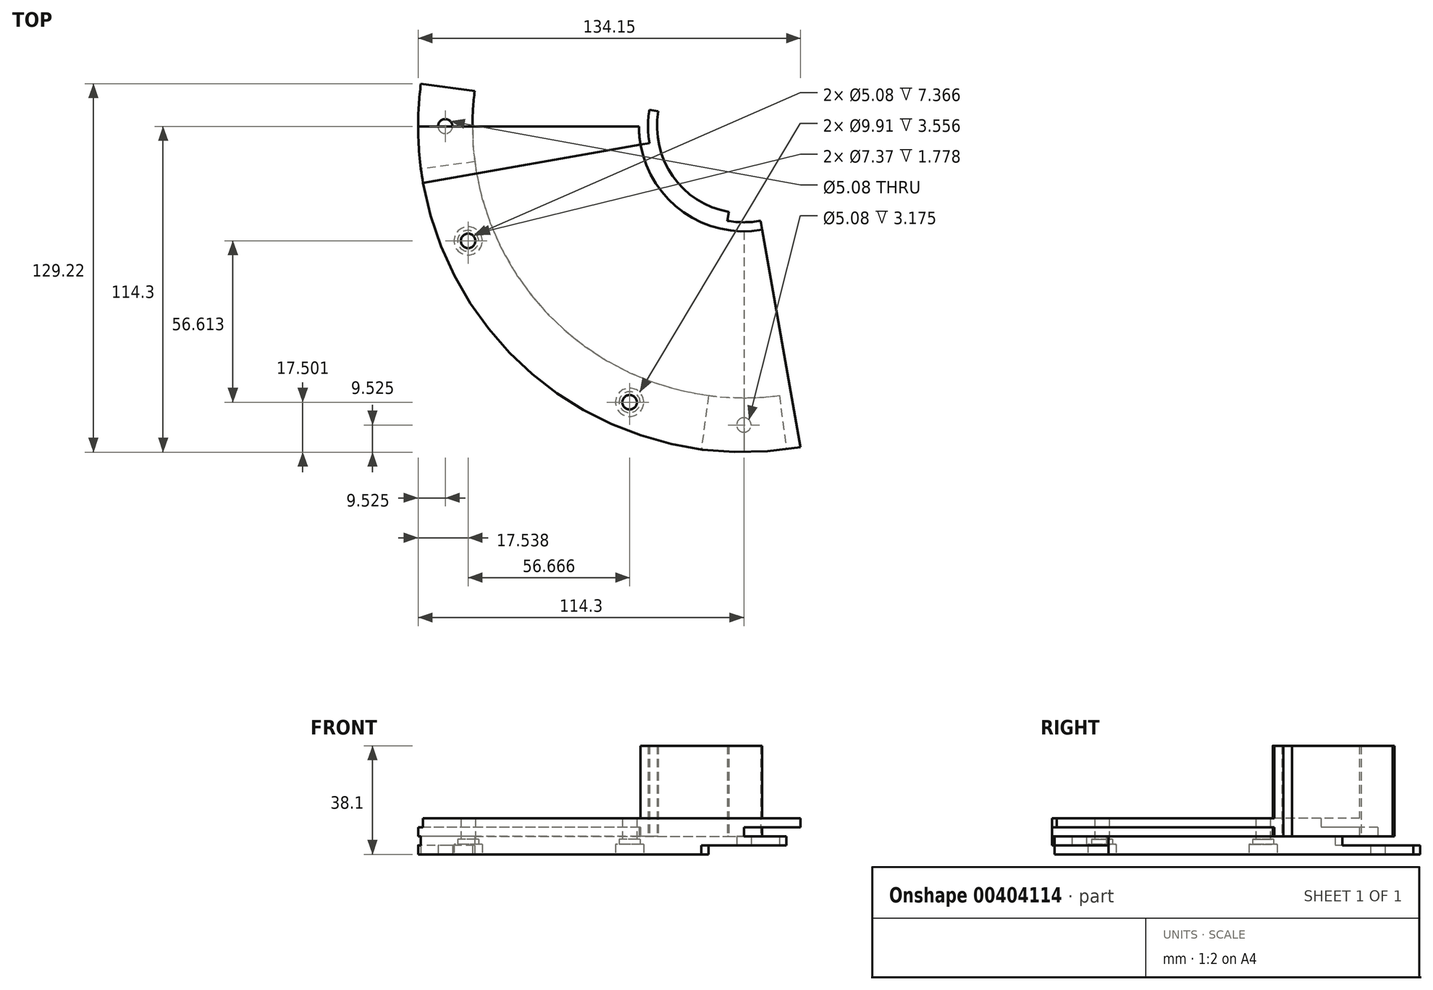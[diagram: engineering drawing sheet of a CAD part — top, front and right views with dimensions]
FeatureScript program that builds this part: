
annotation { "Feature Type Name" : "Feature", "Feature Type Description" : "" }
export const myFeature = defineFeature(function(context is Context, id is Id, definition is map)
    precondition{}
    {
        {
            var Q0;
            Q0=qCreatedBy(makeId("Top.planeOp"),FACE);
            var sketch = newSketch(context, id + "F0", { "sketchPlane" : qUnion([Q0])});
            skCircle(sketch, "E0", {"center": v(0, 0) * mm, "radius": 114.3 * mm});
            skLineSegment(sketch, "E1", {"start": v(0, 114.3) * mm, "end": v(0, -114.3) * mm, "construction": true});
            skLineSegment(sketch, "E2", {"start": v(-114.3, 0) * mm, "end": v(114.3, 0) * mm, "construction": true});
            skCircle(sketch, "E3", {"center": v(0, 0) * mm, "radius": 104.78 * mm, "construction": true});
            skCircle(sketch, "E4", {"center": v(0, 104.78) * mm, "radius": 2.54 * mm});
            skCircle(sketch, "E5", {"center": v(104.78, 0) * mm, "radius": 2.54 * mm});
            skCircle(sketch, "E6", {"center": v(0, -104.78) * mm, "radius": 2.54 * mm});
            skCircle(sketch, "E7", {"center": v(-104.78, 0) * mm, "radius": 2.54 * mm});
            skCircle(sketch, "E8", {"center": v(0, 0) * mm, "radius": 95.25 * mm});
            skLineSegment(sketch, "E9", {"start": v(0.01, -0.1) * mm, "end": v(14.92, -113.32) * mm});
            skLineSegment(sketch, "E10", {"start": v(0, 0) * mm, "end": v(-14.92, -113.32) * mm});
            skLineSegment(sketch, "E11", {"start": v(0, 0) * mm, "end": v(-113.32, -14.92) * mm});
            skLineSegment(sketch, "E12", {"start": v(0, 0) * mm, "end": v(-113.32, 14.92) * mm});
            skLineSegment(sketch, "E13", {"start": v(0.01, -0.1) * mm, "end": v(-105.56, -43.83) * mm, "construction": true});
            skLineSegment(sketch, "E14", {"start": v(0, 0) * mm, "end": v(-43.74, -105.6) * mm, "construction": true});
            skCircle(sketch, "E15", {"center": v(-96.76, -40.19) * mm, "radius": 4.95 * mm});
            skCircle(sketch, "E16", {"center": v(-96.76, -40.19) * mm, "radius": 3.68 * mm});
            skCircle(sketch, "E17", {"center": v(-40.1, -96.8) * mm, "radius": 4.95 * mm});
            skCircle(sketch, "E18", {"center": v(-40.1, -96.8) * mm, "radius": 3.68 * mm});
            skCircle(sketch, "E19", {"center": v(-40.1, -96.8) * mm, "radius": 2.54 * mm});
            skCircle(sketch, "E20", {"center": v(-96.76, -40.19) * mm, "radius": 2.54 * mm});
            skSolve(sketch);
        }
        {
            var Q0;
            {var subQ0=sQuery(id+"F0.wireOp",EDGE,"E10");var subQ1=sQuery(id+"F0.wireOp",EDGE,"E0");var subQ2=makeQuery(id+"F0.imprint","INTERSECT",VERTEX,{"derivedFrom":[subQ1,subQ0]});Q0=makeQuery(id+"F0.imprint","IMPRINT",FACE,{"disambiguationData":[TD([[makeQuery(id+"F0.imprint","IMPRINT",EDGE,{"disambiguationData":[TD([[subQ2,1.0]])],"derivedFrom":subQ1}),1.0]])]});}
            var Q1;
            Q1=makeQuery(id+"F0.imprint","IMPRINT",FACE,{"disambiguationData":[TD([[makeQuery(id+"F0.imprint","IMPRINT",EDGE,{"derivedFrom":sQuery(id+"F0.wireOp",EDGE,"E15")}),1.0]])]});
            var Q2;
            Q2=makeQuery(id+"F0.imprint","IMPRINT",FACE,{"disambiguationData":[TD([[makeQuery(id+"F0.imprint","IMPRINT",EDGE,{"derivedFrom":sQuery(id+"F0.wireOp",EDGE,"E16")}),1.0]])]});
            var Q3;
            Q3=makeQuery(id+"F0.imprint","IMPRINT",FACE,{"disambiguationData":[TD([[makeQuery(id+"F0.imprint","IMPRINT",EDGE,{"derivedFrom":sQuery(id+"F0.wireOp",EDGE,"E17")}),1.0]])]});
            var Q4;
            Q4=makeQuery(id+"F0.imprint","IMPRINT",FACE,{"disambiguationData":[TD([[makeQuery(id+"F0.imprint","IMPRINT",EDGE,{"derivedFrom":sQuery(id+"F0.wireOp",EDGE,"E18")}),1.0]])]});
            extrude(context, id + "F1", {"entities" : qUnion([Q0, Q1, Q2, Q3, Q4]), "depth" : 6.35 * mm});
        }
        {
            var Q0;
            Q0=makeQuery(id+"F0.imprint","IMPRINT",FACE,{"disambiguationData":[TD([[makeQuery(id+"F0.imprint","IMPRINT",EDGE,{"derivedFrom":sQuery(id+"F0.wireOp",EDGE,"E7")}),-1.0]])]});
            extrude(context, id + "F2", {"entities" : qUnion([Q0]), "operationType" : NewBodyOperationType.ADD, "depth" : 3.17 * mm});
        }
        {
            var Q0;
            Q0=makeQuery(id+"F0.imprint","IMPRINT",FACE,{"disambiguationData":[TD([[makeQuery(id+"F0.imprint","IMPRINT",EDGE,{"derivedFrom":sQuery(id+"F0.wireOp",EDGE,"E6")}),-1.0]])]});
            extrude(context, id + "F3", {"entities" : qUnion([Q0]), "operationType" : NewBodyOperationType.ADD, "depth" : 6.35 * mm});
        }
        {
            var Q0;
            Q0=makeQuery(id+"F0.imprint","IMPRINT",FACE,{"disambiguationData":[TD([[makeQuery(id+"F0.imprint","IMPRINT",EDGE,{"derivedFrom":sQuery(id+"F0.wireOp",EDGE,"E6")}),-1.0]])]});
            extrude(context, id + "F4", {"entities" : qUnion([Q0]), "operationType" : NewBodyOperationType.REMOVE, "depth" : 3.17 * mm});
        }
        {
            var Q0;
            Q0=makeQuery(id+"F0.imprint","IMPRINT",FACE,{"disambiguationData":[TD([[makeQuery(id+"F0.imprint","IMPRINT",EDGE,{"derivedFrom":sQuery(id+"F0.wireOp",EDGE,"E17")}),1.0]])]});
            var Q1;
            Q1=makeQuery(id+"F0.imprint","IMPRINT",FACE,{"disambiguationData":[TD([[makeQuery(id+"F0.imprint","IMPRINT",EDGE,{"derivedFrom":sQuery(id+"F0.wireOp",EDGE,"E18")}),1.0]])]});
            extrude(context, id + "F5", {"entities" : qUnion([Q0, Q1]), "operationType" : NewBodyOperationType.REMOVE, "depth" : 3.56 * mm});
        }
        {
            var Q0;
            Q0=makeQuery(id+"F0.imprint","IMPRINT",FACE,{"disambiguationData":[TD([[makeQuery(id+"F0.imprint","IMPRINT",EDGE,{"derivedFrom":sQuery(id+"F0.wireOp",EDGE,"E15")}),1.0]])]});
            var Q1;
            Q1=makeQuery(id+"F0.imprint","IMPRINT",FACE,{"disambiguationData":[TD([[makeQuery(id+"F0.imprint","IMPRINT",EDGE,{"derivedFrom":sQuery(id+"F0.wireOp",EDGE,"E16")}),1.0]])]});
            extrude(context, id + "F6", {"entities" : qUnion([Q0, Q1]), "operationType" : NewBodyOperationType.REMOVE, "depth" : 3.56 * mm});
        }
        {
            var Q0;
            Q0=makeQuery(id+"F0.imprint","IMPRINT",FACE,{"disambiguationData":[TD([[makeQuery(id+"F0.imprint","IMPRINT",EDGE,{"derivedFrom":sQuery(id+"F0.wireOp",EDGE,"E16")}),1.0]])]});
            extrude(context, id + "F7", {"entities" : qUnion([Q0]), "operationType" : NewBodyOperationType.REMOVE, "depth" : 5.33 * mm});
        }
        {
            var Q0;
            Q0=makeQuery(id+"F0.imprint","IMPRINT",FACE,{"disambiguationData":[TD([[makeQuery(id+"F0.imprint","IMPRINT",EDGE,{"derivedFrom":sQuery(id+"F0.wireOp",EDGE,"E18")}),1.0]])]});
            extrude(context, id + "F8", {"entities" : qUnion([Q0]), "operationType" : NewBodyOperationType.REMOVE, "depth" : 5.33 * mm});
        }
        {
            var Q0;
            Q0=makeQuery(id+"F0.imprint","IMPRINT",FACE,{"disambiguationData":[TD([[makeQuery(id+"F0.imprint","IMPRINT",EDGE,{"derivedFrom":sQuery(id+"F0.wireOp",EDGE,"E20")}),1.0]])]});
            extrude(context, id + "F9", {"entities" : qUnion([Q0]), "operationType" : NewBodyOperationType.REMOVE, "depth" : 25.4 * mm});
        }
        {
            var Q0;
            {var subQ0=sQuery(id+"F0.wireOp",EDGE,"E10");var subQ1=sQuery(id+"F0.wireOp",EDGE,"E8");var subQ2=sQuery(id+"F0.wireOp",EDGE,"E0");Q0=makeQuery(id+"F3.boolean.opBoolean","MERGE",FACE,{"derivedFrom":[makeQuery(id+"F1.opExtrude","CAP_FACE",FACE,{"disambiguationData":[OSD([subQ2,subQ1,subQ0,sQuery(id+"F0.wireOp",EDGE,"E11"),sQuery(id+"F0.wireOp",EDGE,"E19"),sQuery(id+"F0.wireOp",EDGE,"E20")])],"isStart":false}),makeQuery(id+"F3.opExtrude","CAP_FACE",FACE,{"disambiguationData":[OSD([subQ2,sQuery(id+"F0.wireOp",EDGE,"E6"),subQ1,sQuery(id+"F0.wireOp",EDGE,"E9"),subQ0])],"isStart":false})]});}
            var sketch = newSketch(context, id + "F10", { "sketchPlane" : qUnion([Q0])});
            skCircle(sketch, "E21.0", {"center": v(0, 0) * mm, "radius": 114.3 * mm});
            skCircle(sketch, "E22.0", {"center": v(-96.76, -40.19) * mm, "radius": 2.54 * mm});
            skCircle(sketch, "E22.1", {"center": v(-40.1, -96.8) * mm, "radius": 2.54 * mm});
            skCircle(sketch, "E23", {"center": v(0, 0) * mm, "radius": 36.83 * mm});
            skCircle(sketch, "E24.0", {"center": v(0, 0) * mm, "radius": 30.48 * mm});
            skLineSegment(sketch, "E25", {"start": v(0, 0) * mm, "end": v(-114.3, 0) * mm, "construction": true});
            skLineSegment(sketch, "E26", {"start": v(0, 0) * mm, "end": v(0, -114.3) * mm, "construction": true});
            skLineSegment(sketch, "E27", {"start": v(-30.48, 0) * mm, "end": v(-114.3, 0) * mm});
            skLineSegment(sketch, "E28", {"start": v(0, -30.48) * mm, "end": v(0, -114.3) * mm});
            skLineSegment(sketch, "E29", {"start": v(0, 0) * mm, "end": v(-112.56, -19.85) * mm});
            skLineSegment(sketch, "E30", {"start": v(0, 0) * mm, "end": v(-19.85, -112.56) * mm});
            skCircle(sketch, "E31.0", {"center": v(0, 0) * mm, "radius": 33.66 * mm});
            skLineSegment(sketch, "E32", {"start": v(0, 0) * mm, "end": v(-112.56, 19.85) * mm});
            skLineSegment(sketch, "E33", {"start": v(0, 0) * mm, "end": v(19.85, -112.56) * mm});
            skSolve(sketch);
        }
        {
            var Q0;
            {var subQ10=makeQuery(id+"F1.opExtrude","CAP_EDGE",EDGE,{"disambiguationData":[OSD([sQuery(id+"F0.wireOp",EDGE,"E11")])],"isStart":false});Q0=makeQuery(id+"F10.imprint","IMPRINT",FACE,{"disambiguationData":[TD([[makeQuery(id+"F10.imprint","IMPRINT",EDGE,{"derivedFrom":subQ10}),-1.0]])]});}
            var Q1;
            Q1=makeQuery(id+"F10.imprint","IMPRINT",FACE,{"disambiguationData":[TD([[makeQuery(id+"F10.imprint","IMPRINT",EDGE,{"derivedFrom":sQuery(id+"F10.wireOp",EDGE,"E22.0")}),-1.0]])]});
            var Q2;
            {var subQ0=sQuery(id+"F10.wireOp",EDGE,"E29");var subQ1=sQuery(id+"F10.wireOp",EDGE,"E23");var subQ2=makeQuery(id+"F10.imprint","INTERSECT",VERTEX,{"derivedFrom":[subQ1,subQ0]});Q2=makeQuery(id+"F10.imprint","IMPRINT",FACE,{"disambiguationData":[TD([[makeQuery(id+"F10.imprint","IMPRINT",EDGE,{"disambiguationData":[TD([[subQ2,-1.0]])],"derivedFrom":subQ1}),-1.0]])]});}
            var Q3;
            {var subQ0=sQuery(id+"F10.wireOp",EDGE,"E29");var subQ1=sQuery(id+"F10.wireOp",EDGE,"E23");var subQ2=makeQuery(id+"F10.imprint","INTERSECT",VERTEX,{"derivedFrom":[subQ1,subQ0]});Q3=makeQuery(id+"F10.imprint","IMPRINT",FACE,{"disambiguationData":[TD([[makeQuery(id+"F10.imprint","IMPRINT",EDGE,{"disambiguationData":[TD([[subQ2,-1.0]])],"derivedFrom":subQ1}),1.0]])]});}
            var Q4;
            {var subQ0=sQuery(id+"F10.wireOp",EDGE,"E29");var subQ1=sQuery(id+"F10.wireOp",EDGE,"E24.0");var subQ2=makeQuery(id+"F10.imprint","INTERSECT",VERTEX,{"derivedFrom":[subQ1,subQ0]});Q4=makeQuery(id+"F10.imprint","IMPRINT",FACE,{"disambiguationData":[TD([[makeQuery(id+"F10.imprint","IMPRINT",EDGE,{"disambiguationData":[TD([[subQ2,-1.0]])],"derivedFrom":subQ1}),-1.0]])]});}
            var Q5;
            {var subQ0=sQuery(id+"F10.wireOp",EDGE,"E30");var subQ1=sQuery(id+"F10.wireOp",EDGE,"E23");var subQ2=makeQuery(id+"F10.imprint","INTERSECT",VERTEX,{"derivedFrom":[subQ1,subQ0]});Q5=makeQuery(id+"F10.imprint","IMPRINT",FACE,{"disambiguationData":[TD([[makeQuery(id+"F10.imprint","IMPRINT",EDGE,{"disambiguationData":[TD([[subQ2,-1.0]])],"derivedFrom":subQ1}),-1.0]])]});}
            var Q6;
            {var subQ0=sQuery(id+"F10.wireOp",EDGE,"E30");var subQ1=sQuery(id+"F10.wireOp",EDGE,"E23");var subQ2=makeQuery(id+"F10.imprint","INTERSECT",VERTEX,{"derivedFrom":[subQ1,subQ0]});Q6=makeQuery(id+"F10.imprint","IMPRINT",FACE,{"disambiguationData":[TD([[makeQuery(id+"F10.imprint","IMPRINT",EDGE,{"disambiguationData":[TD([[subQ2,-1.0]])],"derivedFrom":subQ1}),1.0]])]});}
            var Q7;
            {var subQ0=sQuery(id+"F10.wireOp",EDGE,"E27");var subQ1=sQuery(id+"F10.wireOp",EDGE,"E24.0");var subQ2=makeQuery(id+"F10.imprint","INTERSECT",VERTEX,{"derivedFrom":[subQ1,subQ0]});Q7=makeQuery(id+"F10.imprint","IMPRINT",FACE,{"disambiguationData":[TD([[makeQuery(id+"F10.imprint","IMPRINT",EDGE,{"disambiguationData":[TD([[subQ2,-1.0]])],"derivedFrom":subQ1}),-1.0]])]});}
            var Q8;
            {var subQ1=makeQuery(id+"F1.opExtrude","CAP_EDGE",EDGE,{"disambiguationData":[OSD([sQuery(id+"F0.wireOp",EDGE,"E11")])],"isStart":false});Q8=makeQuery(id+"F10.imprint","IMPRINT",FACE,{"disambiguationData":[TD([[makeQuery(id+"F10.imprint","IMPRINT",EDGE,{"derivedFrom":subQ1}),1.0]])]});}
            var Q9;
            {var subQ1=sQuery(id+"F10.wireOp",EDGE,"E21.0");var subQ6=sQuery(id+"F10.wireOp",EDGE,"E28");var subQ8=makeQuery(id+"F10.imprint","INTERSECT",VERTEX,{"derivedFrom":[subQ1,subQ6]});Q9=makeQuery(id+"F10.imprint","IMPRINT",FACE,{"disambiguationData":[TD([[makeQuery(id+"F10.imprint","IMPRINT",EDGE,{"disambiguationData":[TD([[subQ8,1.0]])],"derivedFrom":subQ1}),1.0]])]});}
            var Q10;
            {var subQ0=sQuery(id+"F10.wireOp",EDGE,"E28");var subQ1=makeQuery(id+"F3.opExtrude","CAP_EDGE",EDGE,{"disambiguationData":[OSD([sQuery(id+"F0.wireOp",EDGE,"E6")])],"isStart":false});var subQ2=makeQuery(id+"F10.imprint","INTERSECT",VERTEX,{"disambiguationData":[OD(0.0)],"derivedFrom":[subQ1,subQ0]});Q10=makeQuery(id+"F10.imprint","IMPRINT",FACE,{"disambiguationData":[TD([[makeQuery(id+"F10.imprint","IMPRINT",EDGE,{"disambiguationData":[TD([[subQ2,-1.0]])],"derivedFrom":subQ0}),-1.0]])]});}
            extrude(context, id + "F11", {"entities" : qUnion([Q0, Q1, Q2, Q3, Q4, Q5, Q6, Q7, Q8, Q9, Q10]), "depth" : 6.35 * mm});
        }
        {
            var Q0;
            {var subQ0=sQuery(id+"F10.wireOp",EDGE,"E27");var subQ1=sQuery(id+"F10.wireOp",EDGE,"E24.0");var subQ2=makeQuery(id+"F10.imprint","INTERSECT",VERTEX,{"derivedFrom":[subQ1,subQ0]});Q0=makeQuery(id+"F10.imprint","IMPRINT",FACE,{"disambiguationData":[TD([[makeQuery(id+"F10.imprint","IMPRINT",EDGE,{"disambiguationData":[TD([[subQ2,-1.0]])],"derivedFrom":subQ1}),-1.0]])]});}
            var Q1;
            {var subQ0=sQuery(id+"F10.wireOp",EDGE,"E29");var subQ1=sQuery(id+"F10.wireOp",EDGE,"E23");var subQ2=makeQuery(id+"F10.imprint","INTERSECT",VERTEX,{"derivedFrom":[subQ1,subQ0]});Q1=makeQuery(id+"F10.imprint","IMPRINT",FACE,{"disambiguationData":[TD([[makeQuery(id+"F10.imprint","IMPRINT",EDGE,{"disambiguationData":[TD([[subQ2,-1.0]])],"derivedFrom":subQ1}),1.0]])]});}
            var Q2;
            {var subQ0=sQuery(id+"F10.wireOp",EDGE,"E29");var subQ1=sQuery(id+"F10.wireOp",EDGE,"E24.0");var subQ2=makeQuery(id+"F10.imprint","INTERSECT",VERTEX,{"derivedFrom":[subQ1,subQ0]});Q2=makeQuery(id+"F10.imprint","IMPRINT",FACE,{"disambiguationData":[TD([[makeQuery(id+"F10.imprint","IMPRINT",EDGE,{"disambiguationData":[TD([[subQ2,-1.0]])],"derivedFrom":subQ1}),-1.0]])]});}
            var Q3;
            {var subQ0=sQuery(id+"F10.wireOp",EDGE,"E30");var subQ1=sQuery(id+"F10.wireOp",EDGE,"E23");var subQ2=makeQuery(id+"F10.imprint","INTERSECT",VERTEX,{"derivedFrom":[subQ1,subQ0]});Q3=makeQuery(id+"F10.imprint","IMPRINT",FACE,{"disambiguationData":[TD([[makeQuery(id+"F10.imprint","IMPRINT",EDGE,{"disambiguationData":[TD([[subQ2,-1.0]])],"derivedFrom":subQ1}),1.0]])]});}
            var Q4;
            {var subQ0=sQuery(id+"F10.wireOp",EDGE,"E27");var subQ1=sQuery(id+"F10.wireOp",EDGE,"E24.0");var subQ2=makeQuery(id+"F10.imprint","INTERSECT",VERTEX,{"derivedFrom":[subQ1,subQ0]});Q4=makeQuery(id+"F10.imprint","IMPRINT",FACE,{"disambiguationData":[TD([[makeQuery(id+"F10.imprint","IMPRINT",EDGE,{"disambiguationData":[TD([[subQ2,1.0]])],"derivedFrom":subQ1}),-1.0]])]});}
            var Q5;
            {var subQ0=sQuery(id+"F10.wireOp",EDGE,"E28");var subQ1=sQuery(id+"F10.wireOp",EDGE,"E23");var subQ2=makeQuery(id+"F10.imprint","INTERSECT",VERTEX,{"derivedFrom":[subQ1,subQ0]});Q5=makeQuery(id+"F10.imprint","IMPRINT",FACE,{"disambiguationData":[TD([[makeQuery(id+"F10.imprint","IMPRINT",EDGE,{"disambiguationData":[TD([[subQ2,-1.0]])],"derivedFrom":subQ1}),1.0]])]});}
            extrude(context, id + "F12", {"entities" : qUnion([Q0, Q1, Q2, Q3, Q4, Q5]), "operationType" : NewBodyOperationType.ADD, "depth" : 31.75 * mm});
        }
        {
            var Q0;
            {var subQ0=sQuery(id+"F10.wireOp",EDGE,"E28");var subQ1=makeQuery(id+"F3.opExtrude","CAP_EDGE",EDGE,{"disambiguationData":[OSD([sQuery(id+"F0.wireOp",EDGE,"E6")])],"isStart":false});var subQ2=makeQuery(id+"F10.imprint","INTERSECT",VERTEX,{"disambiguationData":[OD(0.0)],"derivedFrom":[subQ1,subQ0]});Q0=makeQuery(id+"F10.imprint","IMPRINT",FACE,{"disambiguationData":[TD([[makeQuery(id+"F10.imprint","IMPRINT",EDGE,{"disambiguationData":[TD([[subQ2,-1.0]])],"derivedFrom":subQ0}),1.0]])]});}
            var Q1;
            {var subQ0=makeQuery(id+"F3.opExtrude","CAP_EDGE",EDGE,{"disambiguationData":[OSD([sQuery(id+"F0.wireOp",EDGE,"E9")])],"isStart":false});Q1=makeQuery(id+"F10.imprint","IMPRINT",FACE,{"disambiguationData":[TD([[makeQuery(id+"F10.imprint","IMPRINT",EDGE,{"derivedFrom":subQ0}),-1.0]])]});}
            var Q2;
            {var subQ10=makeQuery(id+"F3.opExtrude","CAP_EDGE",EDGE,{"disambiguationData":[OSD([sQuery(id+"F0.wireOp",EDGE,"E9")])],"isStart":false});Q2=makeQuery(id+"F10.imprint","IMPRINT",FACE,{"disambiguationData":[TD([[makeQuery(id+"F10.imprint","IMPRINT",EDGE,{"derivedFrom":subQ10}),1.0]])]});}
            extrude(context, id + "F13", {"entities" : qUnion([Q0, Q1, Q2]), "operationType" : NewBodyOperationType.ADD, "depth" : 6.35 * mm});
        }
        {
            var Q0;
            {var subQ0=sQuery(id+"F10.wireOp",EDGE,"E28");var subQ1=makeQuery(id+"F3.opExtrude","CAP_EDGE",EDGE,{"disambiguationData":[OSD([sQuery(id+"F0.wireOp",EDGE,"E6")])],"isStart":false});var subQ2=makeQuery(id+"F10.imprint","INTERSECT",VERTEX,{"disambiguationData":[OD(0.0)],"derivedFrom":[subQ1,subQ0]});Q0=makeQuery(id+"F10.imprint","IMPRINT",FACE,{"disambiguationData":[TD([[makeQuery(id+"F10.imprint","IMPRINT",EDGE,{"disambiguationData":[TD([[subQ2,-1.0]])],"derivedFrom":subQ0}),1.0]])]});}
            var Q1;
            {var subQ0=makeQuery(id+"F3.opExtrude","CAP_EDGE",EDGE,{"disambiguationData":[OSD([sQuery(id+"F0.wireOp",EDGE,"E9")])],"isStart":false});Q1=makeQuery(id+"F10.imprint","IMPRINT",FACE,{"disambiguationData":[TD([[makeQuery(id+"F10.imprint","IMPRINT",EDGE,{"derivedFrom":subQ0}),-1.0]])]});}
            var Q2;
            {var subQ10=makeQuery(id+"F3.opExtrude","CAP_EDGE",EDGE,{"disambiguationData":[OSD([sQuery(id+"F0.wireOp",EDGE,"E9")])],"isStart":false});Q2=makeQuery(id+"F10.imprint","IMPRINT",FACE,{"disambiguationData":[TD([[makeQuery(id+"F10.imprint","IMPRINT",EDGE,{"derivedFrom":subQ10}),1.0]])]});}
            extrude(context, id + "F14", {"entities" : qUnion([Q0, Q1, Q2]), "operationType" : NewBodyOperationType.REMOVE, "depth" : 3.17 * mm});
        }
        {
            var Q0;
            {var subQ7=makeQuery(id+"F1.opExtrude","CAP_EDGE",EDGE,{"disambiguationData":[OSD([sQuery(id+"F0.wireOp",EDGE,"E11")])],"isStart":false});Q0=makeQuery(id+"F10.imprint","IMPRINT",FACE,{"disambiguationData":[TD([[makeQuery(id+"F10.imprint","IMPRINT",EDGE,{"derivedFrom":subQ7}),-1.0]])]});}
            var Q1;
            {var subQ1=makeQuery(id+"F1.opExtrude","CAP_EDGE",EDGE,{"disambiguationData":[OSD([sQuery(id+"F0.wireOp",EDGE,"E11")])],"isStart":false});Q1=makeQuery(id+"F10.imprint","IMPRINT",FACE,{"disambiguationData":[TD([[makeQuery(id+"F10.imprint","IMPRINT",EDGE,{"derivedFrom":subQ1}),1.0]])]});}
            extrude(context, id + "F15", {"entities" : qUnion([Q0, Q1]), "operationType" : NewBodyOperationType.REMOVE, "depth" : 6.35 * mm});
        }
        {
            var Q0;
            {var subQ7=makeQuery(id+"F1.opExtrude","CAP_EDGE",EDGE,{"disambiguationData":[OSD([sQuery(id+"F0.wireOp",EDGE,"E11")])],"isStart":false});Q0=makeQuery(id+"F10.imprint","IMPRINT",FACE,{"disambiguationData":[TD([[makeQuery(id+"F10.imprint","IMPRINT",EDGE,{"derivedFrom":subQ7}),-1.0]])]});}
            var Q1;
            {var subQ1=makeQuery(id+"F1.opExtrude","CAP_EDGE",EDGE,{"disambiguationData":[OSD([sQuery(id+"F0.wireOp",EDGE,"E11")])],"isStart":false});Q1=makeQuery(id+"F10.imprint","IMPRINT",FACE,{"disambiguationData":[TD([[makeQuery(id+"F10.imprint","IMPRINT",EDGE,{"derivedFrom":subQ1}),1.0]])]});}
            extrude(context, id + "F16", {"entities" : qUnion([Q0, Q1]), "operationType" : NewBodyOperationType.ADD, "depth" : 3.17 * mm});
        }
    });
